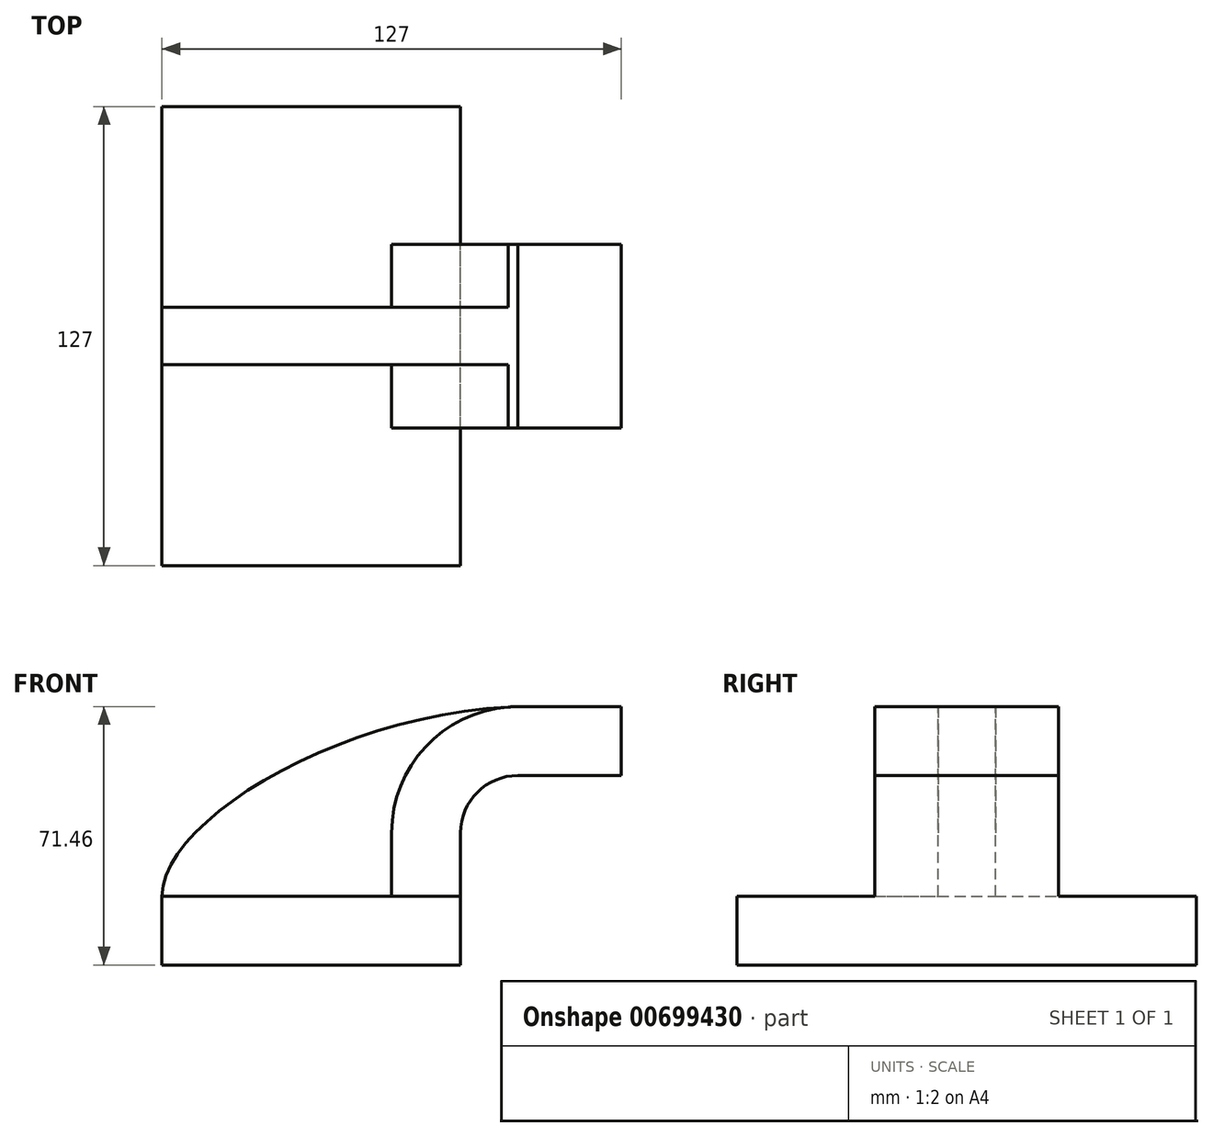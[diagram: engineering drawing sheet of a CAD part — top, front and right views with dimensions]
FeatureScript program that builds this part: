
annotation { "Feature Type Name" : "Feature", "Feature Type Description" : "" }
export const myFeature = defineFeature(function(context is Context, id is Id, definition is map)
    precondition{}
    {
        {
            var Q0;
            Q0=qCreatedBy(makeId("Front.planeOp"),FACE);
            var sketch = newSketch(context, id + "F0", { "sketchPlane" : qUnion([Q0])});
            skLineSegment(sketch, "E0.bottom", {"start": v(-41.28, 9.52) * mm, "end": v(41.27, 9.53) * mm});
            skLineSegment(sketch, "E0.top", {"start": v(-41.28, -9.53) * mm, "end": v(41.28, -9.53) * mm});
            skLineSegment(sketch, "E0.left", {"start": v(-41.28, 9.52) * mm, "end": v(-41.27, -9.53) * mm});
            skLineSegment(sketch, "E0.right", {"start": v(41.28, 9.53) * mm, "end": v(41.28, -9.52) * mm});
            skPoint(sketch, "E0.middle", {"position": v(0, 0) * mm});
            skLineSegment(sketch, "E1.bottom", {"start": v(111.12, 66.68) * mm, "end": v(60.33, 66.68) * mm});
            skLineSegment(sketch, "E1.top", {"start": v(111.12, 38.1) * mm, "end": v(60.33, 38.1) * mm});
            skLineSegment(sketch, "E1.left", {"start": v(111.12, 66.68) * mm, "end": v(111.12, 38.1) * mm});
            skLineSegment(sketch, "E1.right", {"start": v(60.33, 66.68) * mm, "end": v(60.33, 38.1) * mm});
            skPoint(sketch, "E1.middle", {"position": v(85.72, 52.39) * mm});
            skLineSegment(sketch, "E2", {"start": v(41.27, 9.53) * mm, "end": v(41.27, 27) * mm});
            skArc(sketch, "E3", {"start": v(41.27, 27) * mm, "mid": v(45.92, 38.23) * mm, "end": v(57.15, 42.88) * mm});
            skLineSegment(sketch, "E4", {"start": v(57.15, 42.88) * mm, "end": v(86.4, 42.88) * mm});
            skLineSegment(sketch, "E5.0", {"start": v(57.15, 61.93) * mm, "end": v(86.4, 61.93) * mm});
            skArc(sketch, "E5.1", {"start": v(22.22, 27) * mm, "mid": v(32.45, 51.7) * mm, "end": v(57.15, 61.93) * mm});
            skLineSegment(sketch, "E5.2", {"start": v(22.23, 9.53) * mm, "end": v(22.23, 27) * mm});
            skLineSegment(sketch, "E6", {"start": v(85.72, 38.1) * mm, "end": v(85.72, 66.68) * mm});
            skFitSpline(sketch, "E7", {"points": [v(-41.28, 9.53) * mm, v(57.15, 61.93) * mm], "startDerivative": vector(0.91, 65.26) * mm, "endDerivative": vector(141.93, 3.83) * mm});
            skSolve(sketch);
        }
        {
            var Q0;
            Q0=makeQuery(id+"F0.imprint","IMPRINT",FACE,{"disambiguationData":[TD([[makeQuery(id+"F0.imprint","IMPRINT",EDGE,{"derivedFrom":sQuery(id+"F0.wireOp",EDGE,"E0.top")}),1.0]])]});
            extrude(context, id + "F1", {"entities" : qUnion([Q0]), "endBound" : BoundingType.SYMMETRIC, "depth" : 127 * mm, "offsetDistance" : 25.4 * mm});
        }
        {
            var Q0;
            {var subQ1=sQuery(id+"F0.wireOp",EDGE,"E2");Q0=makeQuery(id+"F0.imprint","IMPRINT",FACE,{"disambiguationData":[TD([[makeQuery(id+"F0.imprint","IMPRINT",EDGE,{"derivedFrom":subQ1}),1.0]])]});}
            var Q1;
            {var subQ0=sQuery(id+"F0.wireOp",EDGE,"E5.0");var subQ1=sQuery(id+"F0.wireOp",EDGE,"E1.right");var subQ2=makeQuery(id+"F0.imprint","INTERSECT",VERTEX,{"derivedFrom":[subQ1,subQ0]});Q1=makeQuery(id+"F0.imprint","IMPRINT",FACE,{"disambiguationData":[TD([[makeQuery(id+"F0.imprint","IMPRINT",EDGE,{"disambiguationData":[TD([[subQ2,-1.0]])],"derivedFrom":subQ1}),1.0]])]});}
            extrude(context, id + "F2", {"entities" : qUnion([Q0, Q1]), "operationType" : NewBodyOperationType.ADD, "endBound" : BoundingType.SYMMETRIC, "depth" : 50.8 * mm, "offsetDistance" : 25.4 * mm});
        }
        {
            var Q0;
            {var subQ3=sQuery(id+"F0.wireOp",EDGE,"E5.2");Q0=makeQuery(id+"F0.imprint","IMPRINT",FACE,{"disambiguationData":[TD([[makeQuery(id+"F0.imprint","IMPRINT",EDGE,{"derivedFrom":subQ3}),1.0]])]});}
            extrude(context, id + "F3", {"entities" : qUnion([Q0]), "operationType" : NewBodyOperationType.ADD, "endBound" : BoundingType.SYMMETRIC, "depth" : 15.88 * mm, "offsetDistance" : 25.4 * mm});
        }
    });
